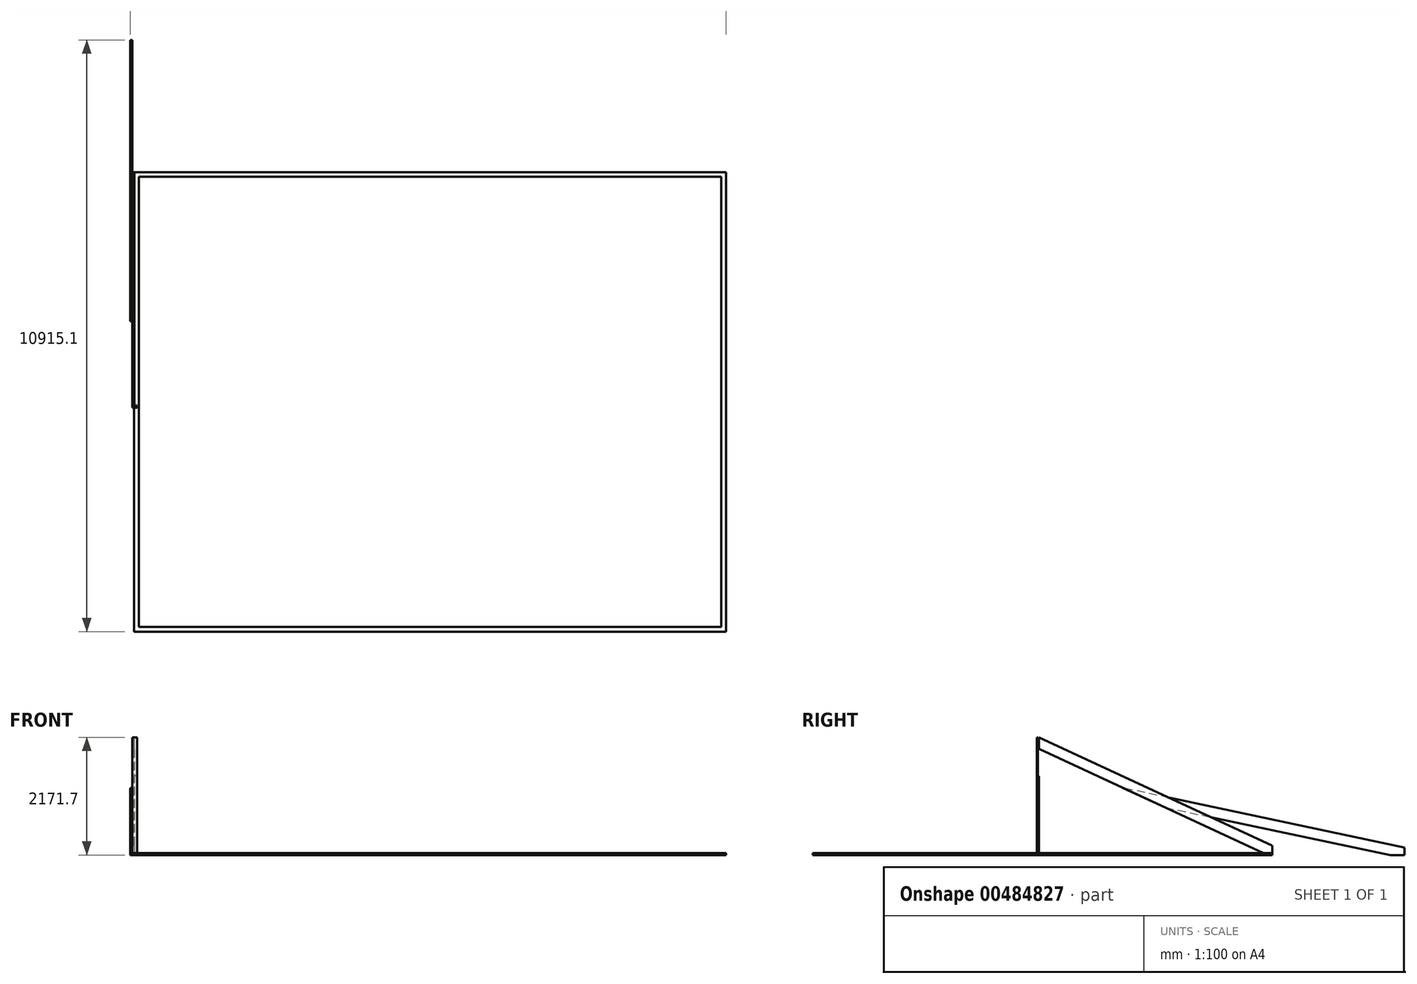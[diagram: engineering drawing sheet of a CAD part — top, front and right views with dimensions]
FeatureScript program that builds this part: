
annotation { "Feature Type Name" : "Feature", "Feature Type Description" : "" }
export const myFeature = defineFeature(function(context is Context, id is Id, definition is map)
    precondition{}
    {
        {
            var Q0;
            Q0=qCreatedBy(makeId("Top.planeOp"),FACE);
            var sketch = newSketch(context, id + "F0", { "sketchPlane" : qUnion([Q0])});
            skLineSegment(sketch, "E0.left", {"start": v(0, 0) * mm, "end": v(34.26, -82.03) * mm});
            skLineSegment(sketch, "E1.bottom", {"start": v(34.26, -82.03) * mm, "end": v(123.16, -82.03) * mm});
            skLineSegment(sketch, "E1.top", {"start": v(34.26, -8387.83) * mm, "end": v(123.16, -8387.83) * mm});
            skLineSegment(sketch, "E1.left", {"start": v(34.26, -82.03) * mm, "end": v(34.26, -8387.83) * mm});
            skLineSegment(sketch, "E1.right", {"start": v(123.16, -82.03) * mm, "end": v(123.16, -8387.83) * mm});
            skLineSegment(sketch, "E2.bottom", {"start": v(34.26, 0) * mm, "end": v(10956.26, 0) * mm});
            skLineSegment(sketch, "E2.top", {"start": v(34.26, -82.03) * mm, "end": v(10956.26, -82.03) * mm});
            skLineSegment(sketch, "E2.left", {"start": v(34.26, 0) * mm, "end": v(34.26, -82.03) * mm});
            skLineSegment(sketch, "E2.right", {"start": v(10956.26, 0) * mm, "end": v(10956.26, -82.03) * mm});
            skLineSegment(sketch, "E3.bottom", {"start": v(34.26, -8387.83) * mm, "end": v(10956.26, -8387.83) * mm});
            skLineSegment(sketch, "E3.top", {"start": v(34.26, -8476.73) * mm, "end": v(10956.26, -8476.73) * mm});
            skLineSegment(sketch, "E3.left", {"start": v(34.26, -8387.83) * mm, "end": v(34.26, -8476.73) * mm});
            skLineSegment(sketch, "E3.right", {"start": v(10956.26, -8387.83) * mm, "end": v(10956.26, -8476.73) * mm});
            skLineSegment(sketch, "E4.bottom", {"start": v(2863.86, -82.03) * mm, "end": v(2774.96, -82.03) * mm});
            skLineSegment(sketch, "E4.top", {"start": v(2829.6, -8387.83) * mm, "end": v(2740.7, -8387.83) * mm});
            skLineSegment(sketch, "E5.bottom", {"start": v(10956.26, -82.03) * mm, "end": v(10867.36, -82.03) * mm});
            skLineSegment(sketch, "E5.top", {"start": v(10956.26, -8387.83) * mm, "end": v(10867.36, -8387.83) * mm});
            skLineSegment(sketch, "E5.left", {"start": v(10956.26, -82.03) * mm, "end": v(10956.26, -8387.83) * mm});
            skLineSegment(sketch, "E5.right", {"start": v(10867.36, -82.03) * mm, "end": v(10867.36, -8387.83) * mm});
            skSolve(sketch);
        }
        {
            var Q0;
            Q0 = qSketchRegion(id + "F0", true);
            extrude(context, id + "F1", {"entities" : qUnion([Q0]), "depth" : 38.1 * mm});
        }
        {
            var Q0;
            Q0=qCreatedBy(makeId("Right.planeOp"),FACE);
            var sketch = newSketch(context, id + "F2", { "sketchPlane" : qUnion([Q0])});
            skLineSegment(sketch, "E6.bottom", {"start": v(-4304.78, 1460.5) * mm, "end": v(-4342.88, 1460.5) * mm});
            skLineSegment(sketch, "E6.top", {"start": v(-4304.78, 38.1) * mm, "end": v(-4342.88, 38.1) * mm});
            skLineSegment(sketch, "E6.left", {"start": v(-4304.78, 1460.5) * mm, "end": v(-4304.78, 38.1) * mm});
            skLineSegment(sketch, "E6.right", {"start": v(-4342.88, 1460.5) * mm, "end": v(-4342.88, 38.1) * mm});
            skLineSegment(sketch, "E7.bottom", {"start": v(-4342.88, 38.1) * mm, "end": v(-4304.78, 38.1) * mm});
            skLineSegment(sketch, "E7.top", {"start": v(-4342.88, 2171.7) * mm, "end": v(-4304.78, 2171.7) * mm});
            skLineSegment(sketch, "E7.left", {"start": v(-4342.88, 38.1) * mm, "end": v(-4342.88, 2171.7) * mm});
            skLineSegment(sketch, "E7.right", {"start": v(-4304.78, 38.1) * mm, "end": v(-4304.78, 2171.7) * mm});
            skLineSegment(sketch, "E8", {"start": v(-4290.85, 1953.1) * mm, "end": v(-82.03, 0) * mm});
            skLineSegment(sketch, "E9", {"start": v(0, 0) * mm, "end": v(0, -132.8) * mm});
            skLineSegment(sketch, "E10", {"start": v(0, 0) * mm, "end": v(309.67, -146.61) * mm});
            skLineSegment(sketch, "E11", {"start": v(-7.22, 177.41) * mm, "end": v(-4304.78, 2171.7) * mm});
            skLineSegment(sketch, "E12", {"start": v(-4304.78, 2171.7) * mm, "end": v(-4304.78, 1961.65) * mm});
            skLineSegment(sketch, "E13", {"start": v(-4304.78, 1961.65) * mm, "end": v(-4290.85, 1953.1) * mm});
            skLineSegment(sketch, "E14", {"start": v(0, 162.56) * mm, "end": v(0, 38.1) * mm});
            skLineSegment(sketch, "E15", {"start": v(0, 38.1) * mm, "end": v(-82.03, 38.1) * mm});
            skLineSegment(sketch, "E16", {"start": v(-82.03, 38.1) * mm, "end": v(-82.03, -0.11) * mm});
            skLineSegment(sketch, "E17", {"start": v(-7.22, 177.41) * mm, "end": v(0, 173.92) * mm});
            skLineSegment(sketch, "E18", {"start": v(0, 162.56) * mm, "end": v(0, 173.92) * mm});
            skLineSegment(sketch, "E19.0.1.0", {"start": v(-4290.85, 1955.03) * mm, "end": v(-82.03, 1.93) * mm});
            skLineSegment(sketch, "E19.0.1.1", {"start": v(-7.22, 179.35) * mm, "end": v(-4304.78, 2173.63) * mm});
            skLineSegment(sketch, "E19.1.0.0", {"start": v(-4292.43, 1953.1) * mm, "end": v(-83.62, 0) * mm});
            skLineSegment(sketch, "E19.1.0.1", {"start": v(-8.8, 177.41) * mm, "end": v(-4306.37, 2171.7) * mm});
            skLineSegment(sketch, "E19.1.1.0", {"start": v(-4292.43, 1955.03) * mm, "end": v(-83.62, 1.93) * mm});
            skLineSegment(sketch, "E19.1.1.1", {"start": v(-8.8, 179.35) * mm, "end": v(-4306.37, 2173.63) * mm});
            skLineSegment(sketch, "E19.2.0.0", {"start": v(-4294.01, 1953.1) * mm, "end": v(-85.2, 0) * mm});
            skLineSegment(sketch, "E19.2.0.1", {"start": v(-10.38, 177.41) * mm, "end": v(-4307.95, 2171.7) * mm});
            skLineSegment(sketch, "E19.2.1.0", {"start": v(-4294.01, 1955.03) * mm, "end": v(-85.2, 1.93) * mm});
            skLineSegment(sketch, "E19.2.1.1", {"start": v(-10.38, 179.35) * mm, "end": v(-4307.95, 2173.63) * mm});
            skLineSegment(sketch, "E19.direction1", {"start": v(-4290.85, 1953.1) * mm, "end": v(-4292.43, 1953.1) * mm, "construction": true});
            skLineSegment(sketch, "E19.direction2", {"start": v(-4290.85, 1953.1) * mm, "end": v(-4290.85, 1955.03) * mm, "construction": true});
            skLineSegment(sketch, "E20", {"start": v(-4323.83, 38.1) * mm, "end": v(-4323.83, 2171.7) * mm});
            skLineSegment(sketch, "E21.MirrorCS", {"start": v(-4353.66, 1953.1) * mm, "end": v(-8562.47, 0) * mm});
            skLineSegment(sketch, "E22.MirrorCS", {"start": v(-8637.29, 177.41) * mm, "end": v(-4339.72, 2171.7) * mm});
            skLineSegment(sketch, "E23.MirrorCS", {"start": v(-4342.88, 2171.7) * mm, "end": v(-4342.88, 1961.65) * mm});
            skLineSegment(sketch, "E24.MirrorCS", {"start": v(-8565.63, 38.1) * mm, "end": v(-8565.63, -0.11) * mm});
            skLineSegment(sketch, "E25.MirrorCS", {"start": v(-8647.67, 38.1) * mm, "end": v(-8565.63, 38.1) * mm});
            skLineSegment(sketch, "E26.MirrorCS", {"start": v(-8647.67, 162.56) * mm, "end": v(-8647.67, 38.1) * mm});
            skLineSegment(sketch, "E27.MirrorCS", {"start": v(-8647.67, 162.56) * mm, "end": v(-8647.67, 173.92) * mm});
            skLineSegment(sketch, "E28.MirrorCS", {"start": v(-8640.45, 177.41) * mm, "end": v(-8647.67, 173.92) * mm});
            skSolve(sketch);
        }
        {
            var Q0;
            Q0=makeQuery(id+"F2.imprint","IMPRINT",FACE,{"disambiguationData":[TD([[makeQuery(id+"F2.imprint","IMPRINT",EDGE,{"derivedFrom":sQuery(id+"F2.wireOp",EDGE,"E8")}),1.0]])]});
            extrude(context, id + "F3", {"entities" : qUnion([Q0]), "operationType" : NewBodyOperationType.ADD, "depth" : 38.1 * mm});
        }
        {
            var Q0;
            Q0=qCreatedBy(makeId("Right.planeOp"),FACE);
            var sketch = newSketch(context, id + "F4", { "sketchPlane" : qUnion([Q0])});
            skLineSegment(sketch, "E29", {"start": v(0, 0) * mm, "end": v(2438.4, 0) * mm});
            skLineSegment(sketch, "E30", {"start": v(0, 0) * mm, "end": v(0, 647.7) * mm});
            skLineSegment(sketch, "E31", {"start": v(2438.4, 0) * mm, "end": v(2438.4, 139.7) * mm});
            skLineSegment(sketch, "E32", {"start": v(2438.4, 139.7) * mm, "end": v(0, 647.7) * mm});
            skLineSegment(sketch, "E33", {"start": v(2438.4, 139.7) * mm, "end": v(-1827.08, 1032.91) * mm});
            skSolve(sketch);
        }
        {
            var Q0;
            Q0 = qSketchRegion(id + "F2", true);
            var sketch = newSketch(context, id + "F5", { "sketchPlane" : qUnion([Q0])});
            skLineSegment(sketch, "E34", {"start": v(2438.4, 0) * mm, "end": v(2438.4, 139.7) * mm});
            skLineSegment(sketch, "E35", {"start": v(2438.4, 139.7) * mm, "end": v(-2754.66, 1236.1) * mm});
            skLineSegment(sketch, "E36", {"start": v(-2754.66, 1236.1) * mm, "end": v(-1966.9, 874.67) * mm});
            skLineSegment(sketch, "E37", {"start": v(-1966.9, 874.67) * mm, "end": v(2175.98, 0) * mm});
            skLineSegment(sketch, "E38", {"start": v(2175.98, 0) * mm, "end": v(2438.4, 0) * mm});
            skLineSegment(sketch, "E39", {"start": v(-4324.75, 42.29) * mm, "end": v(-4324.75, 2171.18) * mm});
            skLineSegment(sketch, "E40.MirrorCS", {"start": v(-6682.6, 874.67) * mm, "end": v(-10825.48, 0) * mm});
            skLineSegment(sketch, "E41.MirrorCS", {"start": v(-11087.9, 139.7) * mm, "end": v(-5894.84, 1236.1) * mm});
            skLineSegment(sketch, "E42.MirrorCS", {"start": v(-10825.48, 0) * mm, "end": v(-11087.9, 0) * mm});
            skLineSegment(sketch, "E43.MirrorCS", {"start": v(-11087.9, 0) * mm, "end": v(-11087.9, 139.7) * mm});
            skLineSegment(sketch, "E44.MirrorCS", {"start": v(-5894.84, 1236.1) * mm, "end": v(-6682.6, 874.67) * mm});
            skSolve(sketch);
        }
        {
            var Q0;
            {var subQ5=sQuery(id+"F5.wireOp",EDGE,"E34");Q0=makeQuery(id+"F5.imprint","IMPRINT",FACE,{"disambiguationData":[TD([[makeQuery(id+"F5.imprint","IMPRINT",EDGE,{"derivedFrom":subQ5}),1.0]])]});}
            var Q1;
            {var subQ0=sQuery(id+"F5.wireOp",EDGE,"E35");var subQ1=makeQuery(id+"F2.imprint","IMPRINT",EDGE,{"derivedFrom":sQuery(id+"F2.wireOp",EDGE,"E11")});var subQ2=makeQuery(id+"F5.imprint","INTERSECT",VERTEX,{"derivedFrom":[subQ1,subQ0]});Q1=makeQuery(id+"F5.imprint","IMPRINT",FACE,{"disambiguationData":[TD([[makeQuery(id+"F5.imprint","IMPRINT",EDGE,{"disambiguationData":[TD([[subQ2,-1.0]])],"derivedFrom":subQ0}),1.0]])]});}
            extrude(context, id + "F6", {"entities" : qUnion([Q0, Q1]), "operationType" : NewBodyOperationType.ADD, "oppositeDirection" : true, "depth" : 38.1 * mm});
        }
        {
            var Q0;
            {var subQ1=sQuery(id+"F2.wireOp",EDGE,"E6.bottom");Q0=makeQuery(id+"F2.imprint","IMPRINT",FACE,{"disambiguationData":[TD([[makeQuery(id+"F2.imprint","IMPRINT",EDGE,{"derivedFrom":subQ1}),-1.0]])]});}
            var Q1;
            {var subQ0=sQuery(id+"F2.wireOp",EDGE,"E6.bottom");Q1=makeQuery(id+"F2.imprint","IMPRINT",FACE,{"disambiguationData":[TD([[makeQuery(id+"F2.imprint","IMPRINT",EDGE,{"derivedFrom":subQ0}),1.0]])]});}
            extrude(context, id + "F7", {"entities" : qUnion([Q0, Q1]), "operationType" : NewBodyOperationType.ADD, "depth" : 88.9 * mm});
        }
    });
